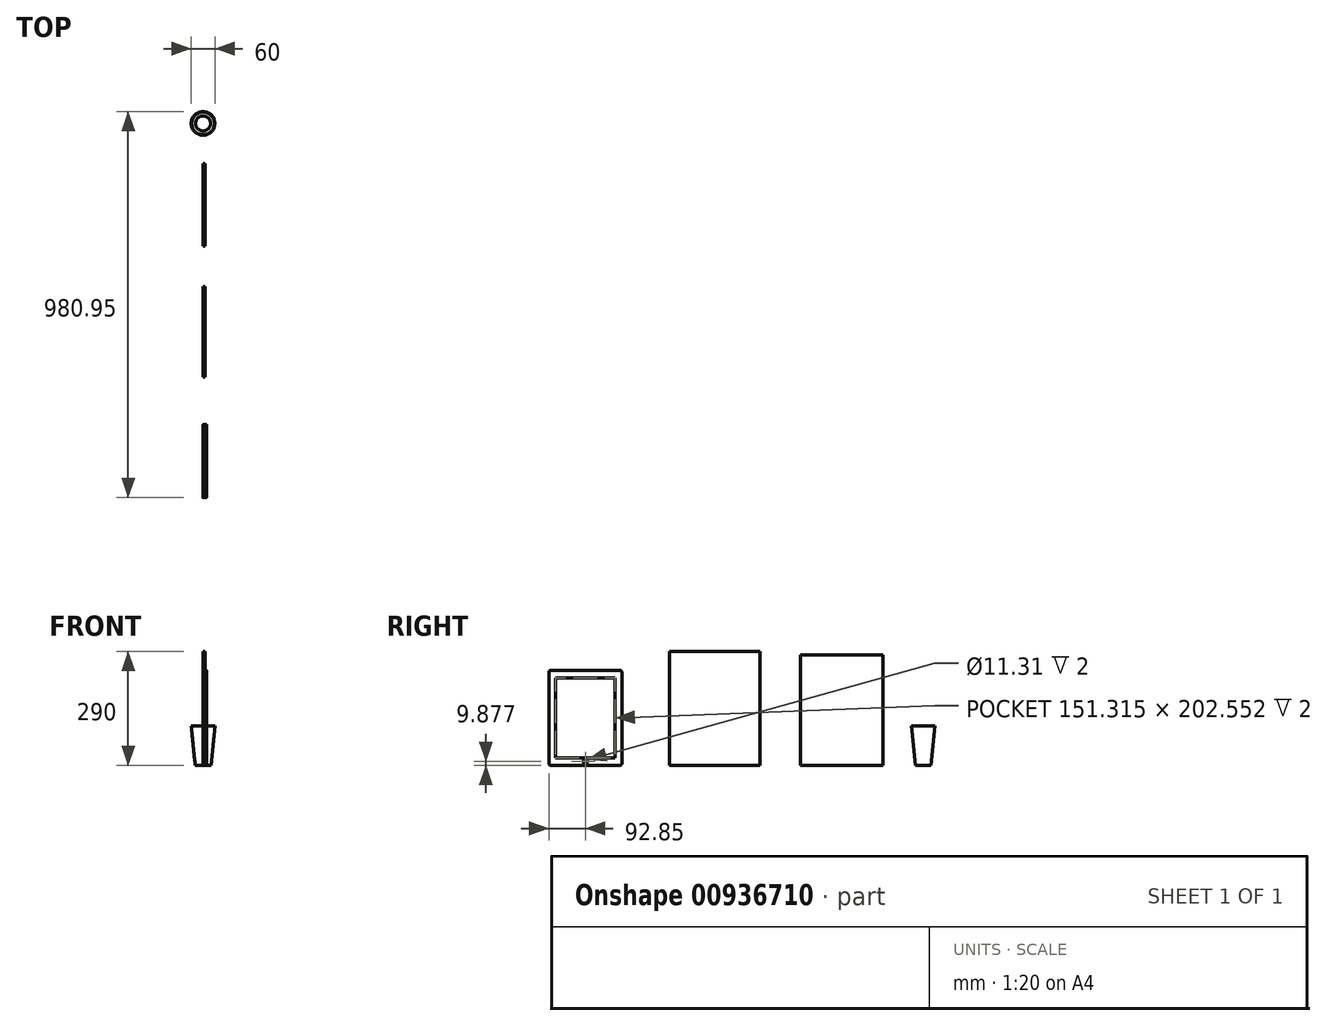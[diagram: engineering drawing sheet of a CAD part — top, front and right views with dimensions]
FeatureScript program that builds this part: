
annotation { "Feature Type Name" : "Feature", "Feature Type Description" : "" }
export const myFeature = defineFeature(function(context is Context, id is Id, definition is map)
    precondition{}
    {
        {
            var Q0;
            Q0=qCreatedBy(makeId("Right.planeOp"),FACE);
            var sketch = newSketch(context, id + "F0", { "sketchPlane" : qUnion([Q0])});
            skLineSegment(sketch, "E0.bottom", {"start": v(0, 0) * mm, "end": v(-185.7, 0) * mm});
            skLineSegment(sketch, "E0.top", {"start": v(0, 241.2) * mm, "end": v(-185.7, 241.2) * mm});
            skLineSegment(sketch, "E0.left", {"start": v(0, 0) * mm, "end": v(0, 241.2) * mm});
            skLineSegment(sketch, "E0.right", {"start": v(-185.7, 0) * mm, "end": v(-185.7, 241.2) * mm});
            skLineSegment(sketch, "E1.bottom", {"start": v(121.13, 0) * mm, "end": v(351.13, 0) * mm});
            skLineSegment(sketch, "E1.top", {"start": v(121.13, 290) * mm, "end": v(351.13, 290) * mm});
            skLineSegment(sketch, "E1.left", {"start": v(121.13, 0) * mm, "end": v(121.13, 290) * mm});
            skLineSegment(sketch, "E1.right", {"start": v(351.13, 0) * mm, "end": v(351.13, 290) * mm});
            skLineSegment(sketch, "E2.bottom", {"start": v(453.12, 0) * mm, "end": v(663.12, 0) * mm});
            skLineSegment(sketch, "E2.top", {"start": v(453.12, 280) * mm, "end": v(663.12, 280) * mm});
            skLineSegment(sketch, "E2.left", {"start": v(453.12, 0) * mm, "end": v(453.12, 280) * mm});
            skLineSegment(sketch, "E2.right", {"start": v(663.12, 0) * mm, "end": v(663.12, 280) * mm});
            skLineSegment(sketch, "E3", {"start": v(765.25, 0) * mm, "end": v(745.25, 0) * mm});
            skLineSegment(sketch, "E4", {"start": v(745.25, 0) * mm, "end": v(735.25, 100) * mm});
            skLineSegment(sketch, "E5", {"start": v(735.25, 100) * mm, "end": v(765.25, 100) * mm});
            skLineSegment(sketch, "E6", {"start": v(765.25, 0) * mm, "end": v(765.25, 100) * mm});
            skSolve(sketch);
        }
        {
            var Q0;
            Q0=makeQuery(id+"F0.imprint","IMPRINT",FACE,{"disambiguationData":[TD([[makeQuery(id+"F0.imprint","IMPRINT",EDGE,{"derivedFrom":sQuery(id+"F0.wireOp",EDGE,"E0.bottom")}),-1.0]])]});
            extrude(context, id + "F1", {"entities" : qUnion([Q0]), "depth" : 8.8 * mm, "offsetDistance" : 25 * mm});
        }
        {
            var Q0;
            Q0=makeQuery(id+"F1.opExtrude","SWEPT_EDGE",EDGE,{"disambiguationData":[OSD([sQuery(id+"F0.wireOp",EDGE,"E0.top"),sQuery(id+"F0.wireOp",EDGE,"E0.right")])]});
            var Q1;
            Q1=makeQuery(id+"F1.opExtrude","SWEPT_EDGE",EDGE,{"disambiguationData":[OSD([sQuery(id+"F0.wireOp",EDGE,"E0.top"),sQuery(id+"F0.wireOp",EDGE,"E0.left")])]});
            var Q2;
            Q2=makeQuery(id+"F1.opExtrude","SWEPT_EDGE",EDGE,{"disambiguationData":[OSD([sQuery(id+"F0.wireOp",EDGE,"E0.bottom"),sQuery(id+"F0.wireOp",EDGE,"E0.right")])]});
            var Q3;
            Q3=makeQuery(id+"F1.opExtrude","SWEPT_EDGE",EDGE,{"disambiguationData":[OSD([sQuery(id+"F0.wireOp",EDGE,"E0.bottom"),sQuery(id+"F0.wireOp",EDGE,"E0.left")])]});
            fillet(context, id + "F2", {"entities" : qUnion([Q0, Q1, Q2, Q3]), "radius" : 5 * mm, "tangentPropagation" : true, "allowEdgeOverflow" : false});
        }
        {
            var Q0;
            Q0=makeQuery(id+"F1.opExtrude","CAP_FACE",FACE,{"disambiguationData":[OSD([sQuery(id+"F0.wireOp",EDGE,"E0.bottom"),sQuery(id+"F0.wireOp",EDGE,"E0.top"),sQuery(id+"F0.wireOp",EDGE,"E0.left"),sQuery(id+"F0.wireOp",EDGE,"E0.right")])],"isStart":false});
            var sketch = newSketch(context, id + "F3", { "sketchPlane" : qUnion([Q0])});
            skLineSegment(sketch, "E7.bottom", {"start": v(-168.5, 221.88) * mm, "end": v(-17.2, 221.88) * mm});
            skLineSegment(sketch, "E7.top", {"start": v(-168.5, 19.32) * mm, "end": v(-17.2, 19.32) * mm});
            skLineSegment(sketch, "E7.left", {"start": v(-168.5, 221.88) * mm, "end": v(-168.5, 19.32) * mm});
            skLineSegment(sketch, "E7.right", {"start": v(-17.2, 221.88) * mm, "end": v(-17.2, 19.32) * mm});
            skPoint(sketch, "E8", {"position": v(-92.85, 241.2) * mm});
            skPoint(sketch, "E9", {"position": v(-92.85, 221.88) * mm});
            skPoint(sketch, "E10", {"position": v(-168.5, 120.6) * mm});
            skPoint(sketch, "E11", {"position": v(-185.7, 120.6) * mm});
            skCircle(sketch, "E12", {"center": v(-92.85, 9.88) * mm, "radius": 5.65 * mm});
            skPoint(sketch, "E12.centerSnap0", {"position": v(-92.85, 19.32) * mm});
            skSolve(sketch);
        }
        {
            var Q0;
            Q0=makeQuery(id+"F3.imprint","IMPRINT",FACE,{"disambiguationData":[TD([[makeQuery(id+"F3.imprint","IMPRINT",EDGE,{"derivedFrom":sQuery(id+"F3.wireOp",EDGE,"E7.bottom")}),-1.0]])]});
            var Q1;
            Q1=makeQuery(id+"F3.imprint","IMPRINT",FACE,{"disambiguationData":[TD([[makeQuery(id+"F3.imprint","IMPRINT",EDGE,{"derivedFrom":sQuery(id+"F3.wireOp",EDGE,"E12")}),1.0]])]});
            extrude(context, id + "F4", {"entities" : qUnion([Q0, Q1]), "oppositeDirection" : true, "depth" : 2 * mm, "offsetDistance" : 25 * mm});
        }
        {
            var Q0;
            Q0=makeQuery(id+"F4.opExtrude","SWEPT_BODY",BODY,{"disambiguationData":[OSD([sQuery(id+"F3.wireOp",EDGE,"E7.bottom"),sQuery(id+"F3.wireOp",EDGE,"E7.top"),sQuery(id+"F3.wireOp",EDGE,"E7.left"),sQuery(id+"F3.wireOp",EDGE,"E7.right")])]});
            var Q1;
            Q1=makeQuery(id+"F4.opExtrude","SWEPT_BODY",BODY,{"disambiguationData":[OSD([sQuery(id+"F3.wireOp",EDGE,"E12")])]});
            var Q2;
            Q2=makeQuery(id+"F1.opExtrude","SWEPT_BODY",BODY,{"disambiguationData":[OSD([sQuery(id+"F0.wireOp",EDGE,"E0.bottom"),sQuery(id+"F0.wireOp",EDGE,"E0.top"),sQuery(id+"F0.wireOp",EDGE,"E0.left"),sQuery(id+"F0.wireOp",EDGE,"E0.right")])]});
            booleanBodies(context, id + "F5", {"operationType" : BooleanOperationType.SUBTRACTION, "tools" : qUnion([Q0, Q1]), "targets" : qUnion([Q2]), "keepTools" : true});
        }
        {
            var Q0;
            Q0=makeQuery(id+"F0.imprint","IMPRINT",FACE,{"disambiguationData":[TD([[makeQuery(id+"F0.imprint","IMPRINT",EDGE,{"derivedFrom":sQuery(id+"F0.wireOp",EDGE,"E1.bottom")}),1.0]])]});
            var Q1;
            Q1=makeQuery(id+"F0.imprint","IMPRINT",FACE,{"disambiguationData":[TD([[makeQuery(id+"F0.imprint","IMPRINT",EDGE,{"derivedFrom":sQuery(id+"F0.wireOp",EDGE,"E2.bottom")}),1.0]])]});
            extrude(context, id + "F6", {"entities" : qUnion([Q0, Q1]), "depth" : 5 * mm, "offsetDistance" : 25 * mm});
        }
        {
            var Q0;
            Q0=makeQuery(id+"F0.imprint","IMPRINT",FACE,{"disambiguationData":[TD([[makeQuery(id+"F0.imprint","IMPRINT",EDGE,{"derivedFrom":sQuery(id+"F0.wireOp",EDGE,"E3")}),-1.0]])]});
            var Q1;
            Q1=sQuery(id+"F0.wireOp",EDGE,"E6");
            revolve(context, id + "F7", {"surfaceOperationType" : NewSurfaceOperationType.NEW, "entities" : qUnion([Q0]), "axis" : qUnion([Q1]), "revolveType" : RevolveType.FULL});
        }
        {
            var Q0;
            Q0=makeQuery(id+"F7.opRevolve","SWEPT_FACE",FACE,{"disambiguationData":[OSD([sQuery(id+"F0.wireOp",EDGE,"E5")])]});
            shell(context, id + "F8", {"entities" : qUnion([Q0]), "thickness" : 1 * mm});
        }
    });
